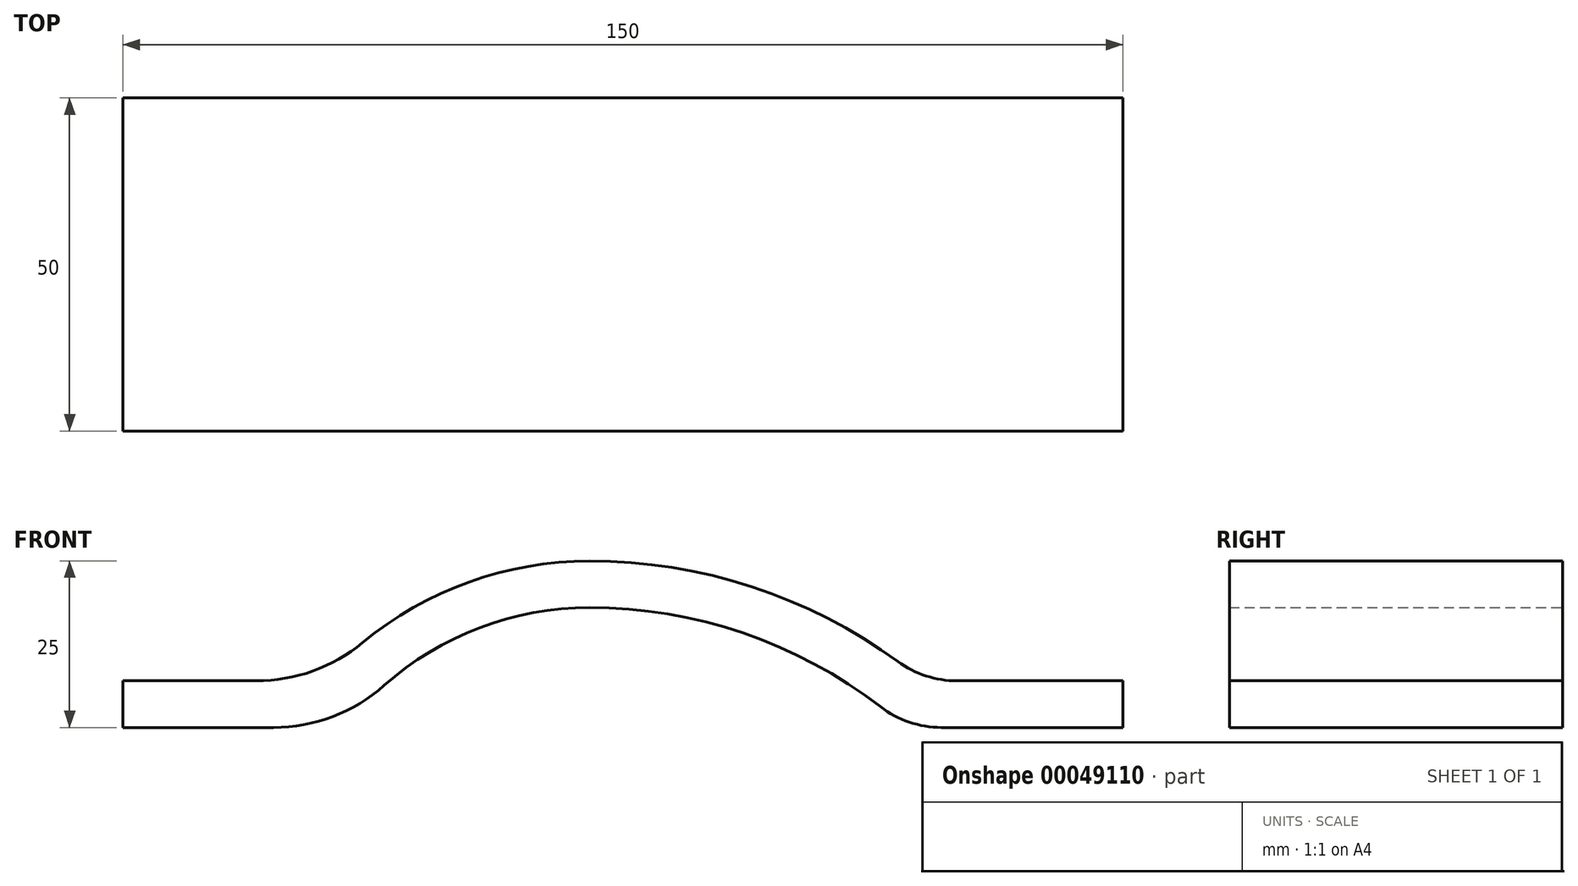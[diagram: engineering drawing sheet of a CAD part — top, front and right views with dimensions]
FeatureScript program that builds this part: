
annotation { "Feature Type Name" : "Feature", "Feature Type Description" : "" }
export const myFeature = defineFeature(function(context is Context, id is Id, definition is map)
    precondition{}
    {
        {
            assignVariable(context, id + "F0", {"name" : "ra", "anyValue" : 25 * mm});
        }
        {
            assignVariable(context, id + "F1", {"name" : "rb", "anyValue" : 15 * mm});
        }
        {
            assignVariable(context, id + "F2", {"name" : "a", "anyValue" : 50 * mm});
        }
        {
            var Q0;
            Q0=qCreatedBy(makeId("Front.planeOp"),FACE);
            var sketch = newSketch(context, id + "F3", { "sketchPlane" : qUnion([Q0])});
            skLineSegment(sketch, "E0", {"start": v(0, 0) * mm, "end": v(-70, 0) * mm});
            skLineSegment(sketch, "E1", {"start": v(-70, 0) * mm, "end": v(-70, 7) * mm});
            skLineSegment(sketch, "E2", {"start": v(-70, 7) * mm, "end": v(-40, 7) * mm});
            skLineSegment(sketch, "E3", {"start": v(-40, 7) * mm, "end": v(50, 7) * mm});
            skLineSegment(sketch, "E4", {"start": v(50, 7) * mm, "end": v(80, 7) * mm});
            skLineSegment(sketch, "E5", {"start": v(80, 7) * mm, "end": v(80, 0) * mm});
            skLineSegment(sketch, "E6", {"start": v(80, 0) * mm, "end": v(0, 0) * mm});
            skLineSegment(sketch, "E7", {"start": v(-46.56, 25) * mm, "end": v(64.84, 25) * mm, "construction": true});
            skSolve(sketch);
        }
        {
            var Q0;
            Q0=qCreatedBy(makeId("Front.planeOp"),FACE);
            var sketch = newSketch(context, id + "F4", { "sketchPlane" : qUnion([Q0])});
            skLineSegment(sketch, "E8.0", {"start": v(-46.56, 25) * mm, "end": v(64.84, 25) * mm, "construction": true});
            skPoint(sketch, "E9.0", {"position": v(-40, 7) * mm});
            skArc(sketch, "E10", {"start": v(0, 25) * mm, "mid": v(-53.44, -28.44) * mm, "end": v(0, -81.89) * mm});
            skPoint(sketch, "E10.first.point", {"position": v(0, 25) * mm});
            skArc(sketch, "E11", {"start": v(0, 18) * mm, "mid": v(-46.44, -28.44) * mm, "end": v(0, -74.89) * mm});
            skLineSegment(sketch, "E12", {"start": v(0, 25) * mm, "end": v(0, -81.89) * mm});
            skLineSegment(sketch, "E13.0", {"start": v(0, 0) * mm, "end": v(-70, 0) * mm});
            skSolve(sketch);
        }
        {
            var Q0;
            Q0=qCreatedBy(makeId("Front.planeOp"),FACE);
            var sketch = newSketch(context, id + "F5", { "sketchPlane" : qUnion([Q0])});
            skLineSegment(sketch, "E14.0", {"start": v(-46.56, 25) * mm, "end": v(64.84, 25) * mm, "construction": true});
            skPoint(sketch, "E15.0", {"position": v(50, 7) * mm});
            skArc(sketch, "E16", {"start": v(0, -131.89) * mm, "mid": v(78.44, -53.44) * mm, "end": v(0, 25) * mm});
            skArc(sketch, "E17", {"start": v(0, -124.89) * mm, "mid": v(71.44, -53.44) * mm, "end": v(0, 18) * mm});
            skLineSegment(sketch, "E18", {"start": v(0, 25) * mm, "end": v(0, -131.89) * mm});
            skLineSegment(sketch, "E19.0", {"start": v(80, 0) * mm, "end": v(0, 0) * mm});
            skSolve(sketch);
        }
        {
            var Q0;
            Q0=makeQuery(id+"F3.imprint","IMPRINT",FACE,{"disambiguationData":[TD([[makeQuery(id+"F3.imprint","IMPRINT",EDGE,{"derivedFrom":sQuery(id+"F3.wireOp",EDGE,"E0")}),-1.0]])]});
            extrude(context, id + "F6", {"entities" : qUnion([Q0]), "endBound" : BoundingType.SYMMETRIC, "depth" : getVariable(context, 'a')});
        }
        {
            var Q0;
            {var subQ3=sQuery(id+"F4.wireOp",EDGE,"E10");var subQ5=sQuery(id+"F4.wireOp",EDGE,"E12");var subQ7=makeQuery(id+"F4.imprint","INTERSECT",VERTEX,{"disambiguationData":[OD(0.0)],"derivedFrom":[subQ3,subQ5]});Q0=makeQuery(id+"F4.imprint","IMPRINT",FACE,{"disambiguationData":[TD([[makeQuery(id+"F4.imprint","IMPRINT",EDGE,{"disambiguationData":[TD([[subQ7,-1.0]])],"derivedFrom":subQ3}),1.0]])]});}
            extrude(context, id + "F7", {"entities" : qUnion([Q0]), "operationType" : NewBodyOperationType.ADD, "endBound" : BoundingType.SYMMETRIC, "depth" : getVariable(context, 'a')});
        }
        {
            var Q0;
            {var subQ3=sQuery(id+"F5.wireOp",EDGE,"E16");var subQ5=sQuery(id+"F5.wireOp",EDGE,"E18");var subQ7=makeQuery(id+"F5.imprint","INTERSECT",VERTEX,{"disambiguationData":[OD(1.0)],"derivedFrom":[subQ3,subQ5]});Q0=makeQuery(id+"F5.imprint","IMPRINT",FACE,{"disambiguationData":[TD([[makeQuery(id+"F5.imprint","IMPRINT",EDGE,{"disambiguationData":[TD([[subQ7,1.0]])],"derivedFrom":subQ3}),1.0]])]});}
            extrude(context, id + "F8", {"entities" : qUnion([Q0]), "operationType" : NewBodyOperationType.ADD, "endBound" : BoundingType.SYMMETRIC, "depth" : getVariable(context, 'a')});
        }
        {
            var Q0;
            {var subQ1=sQuery(id+"F4.wireOp",EDGE,"E11");Q0=makeQuery(id+"F4.imprint","IMPRINT",FACE,{"disambiguationData":[TD([[makeQuery(id+"F4.imprint","IMPRINT",EDGE,{"derivedFrom":subQ1}),1.0]])]});}
            extrude(context, id + "F9", {"entities" : qUnion([Q0]), "operationType" : NewBodyOperationType.REMOVE, "endBound" : BoundingType.SYMMETRIC, "oppositeDirection" : true, "depth" : getVariable(context, 'a')});
        }
        {
            var Q0;
            {var subQ1=sQuery(id+"F5.wireOp",EDGE,"E17");Q0=makeQuery(id+"F5.imprint","IMPRINT",FACE,{"disambiguationData":[TD([[makeQuery(id+"F5.imprint","IMPRINT",EDGE,{"derivedFrom":subQ1}),1.0]])]});}
            extrude(context, id + "F10", {"entities" : qUnion([Q0]), "operationType" : NewBodyOperationType.REMOVE, "endBound" : BoundingType.SYMMETRIC, "oppositeDirection" : true, "depth" : getVariable(context, 'a')});
        }
        {
            var Q0;
            Q0=makeQuery(id+"F7.boolean.opBoolean","INTERSECT",EDGE,{"derivedFrom":[makeQuery(id+"F6.opExtrude","SWEPT_FACE",FACE,{"disambiguationData":[OSD([sQuery(id+"F3.wireOp",EDGE,"E2"),sQuery(id+"F3.wireOp",EDGE,"E3"),sQuery(id+"F3.wireOp",EDGE,"E4")])]}),makeQuery(id+"F7.opExtrude","SWEPT_FACE",FACE,{"disambiguationData":[OSD([sQuery(id+"F4.wireOp",EDGE,"E10")])]})]});
            var Q1;
            Q1=makeQuery(id+"F9.boolean.opBoolean","INTERSECT",EDGE,{"derivedFrom":[makeQuery(id+"F6.opExtrude","SWEPT_FACE",FACE,{"disambiguationData":[OSD([sQuery(id+"F3.wireOp",EDGE,"E0"),sQuery(id+"F3.wireOp",EDGE,"E6")])]}),makeQuery(id+"F9.opExtrude","SWEPT_FACE",FACE,{"disambiguationData":[OSD([sQuery(id+"F4.wireOp",EDGE,"E11")])]})]});
            fillet(context, id + "F11", {"entities" : qUnion([Q0, Q1]), "radius" : getVariable(context, 'ra'), "tangentPropagation" : true, "allowEdgeOverflow" : false});
        }
        {
            var Q0;
            {var subQ0=sQuery(id+"F3.wireOp",EDGE,"E2");var subQ1=sQuery(id+"F3.wireOp",EDGE,"E3");var subQ2=sQuery(id+"F3.wireOp",EDGE,"E4");var subQ9=sQuery(id+"F3.wireOp",EDGE,"E5");Q0=makeQuery(id+"F8.boolean.opBoolean","INTERSECT",EDGE,{"derivedFrom":[makeQuery(id+"F7.boolean.opBoolean","SPLIT",FACE,{"disambiguationData":[TD([makeQuery(id+"F6.opExtrude","SWEPT_FACE",FACE,{"disambiguationData":[OSD([subQ9])]})])],"derivedFrom":makeQuery(id+"F6.opExtrude","SWEPT_FACE",FACE,{"disambiguationData":[OSD([subQ0,subQ1,subQ2])]})}),makeQuery(id+"F8.opExtrude","SWEPT_FACE",FACE,{"disambiguationData":[OSD([sQuery(id+"F5.wireOp",EDGE,"E16")])]})]});}
            var Q1;
            {var subQ0=sQuery(id+"F3.wireOp",EDGE,"E0");var subQ1=sQuery(id+"F3.wireOp",EDGE,"E6");var subQ3=sQuery(id+"F5.wireOp",EDGE,"E17");var subQ14=sQuery(id+"F3.wireOp",EDGE,"E5");Q1=makeQuery(id+"F10.boolean.opBoolean","INTERSECT",EDGE,{"derivedFrom":[makeQuery(id+"F9.boolean.opBoolean","SPLIT",FACE,{"disambiguationData":[TD([makeQuery(id+"F6.opExtrude","SWEPT_FACE",FACE,{"disambiguationData":[OSD([subQ14])]})])],"derivedFrom":makeQuery(id+"F6.opExtrude","SWEPT_FACE",FACE,{"disambiguationData":[OSD([subQ0,subQ1])]})}),makeQuery(id+"F10.opExtrude","SWEPT_FACE",FACE,{"disambiguationData":[OSD([subQ3])]})]});}
            fillet(context, id + "F12", {"entities" : qUnion([Q0, Q1]), "radius" : getVariable(context, 'rb'), "tangentPropagation" : true, "allowEdgeOverflow" : false});
        }
    });
